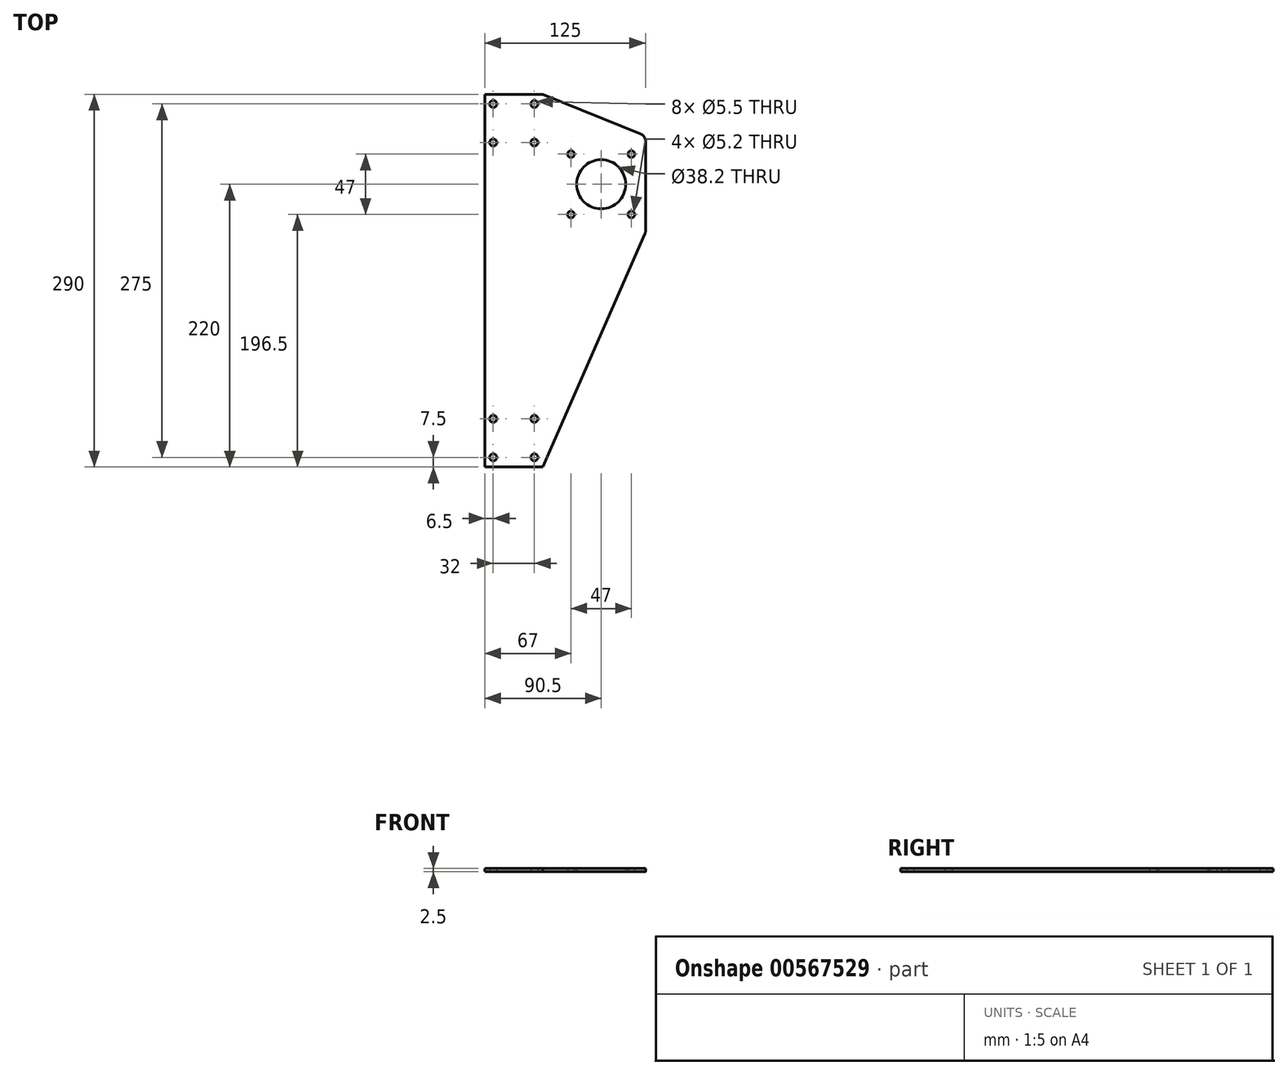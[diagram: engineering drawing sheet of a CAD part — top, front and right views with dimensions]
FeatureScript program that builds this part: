
annotation { "Feature Type Name" : "Feature", "Feature Type Description" : "" }
export const myFeature = defineFeature(function(context is Context, id is Id, definition is map)
    precondition{}
    {
        {
            var Q0;
            Q0=qCreatedBy(makeId("Top.planeOp"),FACE);
            var sketch = newSketch(context, id + "F0", { "sketchPlane" : qUnion([Q0])});
            skLineSegment(sketch, "E0", {"start": v(0, 70) * mm, "end": v(-22.5, 70) * mm});
            skLineSegment(sketch, "E1", {"start": v(-22.5, 70) * mm, "end": v(-22.5, 0) * mm});
            skLineSegment(sketch, "E2", {"start": v(-22.5, 0) * mm, "end": v(-22.5, -220) * mm});
            skLineSegment(sketch, "E3", {"start": v(-22.5, -220) * mm, "end": v(22.5, -220) * mm});
            skLineSegment(sketch, "E4", {"start": v(22.5, -220) * mm, "end": v(102, -38.7) * mm});
            skLineSegment(sketch, "E5", {"start": v(102.5, -36.29) * mm, "end": v(102.5, 33.64) * mm});
            skLineSegment(sketch, "E6", {"start": v(98.75, 39.2) * mm, "end": v(22.5, 70) * mm});
            skLineSegment(sketch, "E7", {"start": v(22.5, 70) * mm, "end": v(0, 70) * mm});
            skPoint(sketch, "E8.visualSharp", {"position": v(102.5, 37.69) * mm});
            skArc(sketch, "E8.filletArc", {"start": v(102.5, 33.64) * mm, "mid": v(101.47, 37) * mm, "end": v(98.75, 39.2) * mm});
            skPoint(sketch, "E9.visualSharp", {"position": v(102.5, -37.55) * mm});
            skArc(sketch, "E9.filletArc", {"start": v(102, -38.7) * mm, "mid": v(102.37, -37.52) * mm, "end": v(102.5, -36.29) * mm});
            skSolve(sketch);
        }
        {
            var Q0;
            Q0=qCreatedBy(makeId("Top.planeOp"),FACE);
            var sketch = newSketch(context, id + "F1", { "sketchPlane" : qUnion([Q0])});
            skCircle(sketch, "E10", {"center": v(68, 0) * mm, "radius": 19.1 * mm});
            skCircle(sketch, "E11", {"center": v(44.5, 23.5) * mm, "radius": 2.6 * mm});
            skCircle(sketch, "E12.MirrorC", {"center": v(44.5, -23.5) * mm, "radius": 2.6 * mm});
            skCircle(sketch, "E13", {"center": v(91.5, 23.5) * mm, "radius": 2.6 * mm});
            skCircle(sketch, "E14.MirrorC", {"center": v(91.5, -23.5) * mm, "radius": 2.6 * mm});
            skLineSegment(sketch, "E15.bottom", {"start": v(91.5, 23.5) * mm, "end": v(44.5, 23.5) * mm, "construction": true});
            skLineSegment(sketch, "E15.top", {"start": v(91.5, -23.5) * mm, "end": v(44.5, -23.5) * mm, "construction": true});
            skLineSegment(sketch, "E15.left", {"start": v(91.5, 23.5) * mm, "end": v(91.5, -23.5) * mm, "construction": true});
            skLineSegment(sketch, "E15.right", {"start": v(44.5, 23.5) * mm, "end": v(44.5, -23.5) * mm, "construction": true});
            skSolve(sketch);
        }
        {
            var Q0;
            Q0=qCreatedBy(makeId("Top.planeOp"),FACE);
            var sketch = newSketch(context, id + "F2", { "sketchPlane" : qUnion([Q0])});
            skCircle(sketch, "E16", {"center": v(-16, 62.5) * mm, "radius": 2.75 * mm});
            skCircle(sketch, "E17", {"center": v(-16, 32.5) * mm, "radius": 2.75 * mm});
            skCircle(sketch, "E18.MirrorC", {"center": v(16, 62.5) * mm, "radius": 2.75 * mm});
            skCircle(sketch, "E19.MirrorC", {"center": v(16, 32.5) * mm, "radius": 2.75 * mm});
            skLineSegment(sketch, "E20.bottom", {"start": v(-16, 32.5) * mm, "end": v(16, 32.5) * mm, "construction": true});
            skLineSegment(sketch, "E20.top", {"start": v(-16, 62.5) * mm, "end": v(16, 62.5) * mm, "construction": true});
            skLineSegment(sketch, "E20.left", {"start": v(-16, 32.5) * mm, "end": v(-16, 62.5) * mm, "construction": true});
            skLineSegment(sketch, "E20.right", {"start": v(16, 32.5) * mm, "end": v(16, 62.5) * mm, "construction": true});
            skSolve(sketch);
        }
        {
            var Q0;
            Q0=qCreatedBy(makeId("Top.planeOp"),FACE);
            var sketch = newSketch(context, id + "F3", { "sketchPlane" : qUnion([Q0])});
            skCircle(sketch, "E21", {"center": v(-16, -212.5) * mm, "radius": 2.75 * mm});
            skLineSegment(sketch, "E22.bottom", {"start": v(-16, -212.5) * mm, "end": v(16, -212.5) * mm, "construction": true});
            skLineSegment(sketch, "E22.top", {"start": v(-16, -182.5) * mm, "end": v(16, -182.5) * mm, "construction": true});
            skLineSegment(sketch, "E22.left", {"start": v(-16, -212.5) * mm, "end": v(-16, -182.5) * mm, "construction": true});
            skLineSegment(sketch, "E22.right", {"start": v(16, -212.5) * mm, "end": v(16, -182.5) * mm, "construction": true});
            skCircle(sketch, "E23.0.1.0", {"center": v(-16, -182.5) * mm, "radius": 2.75 * mm});
            skCircle(sketch, "E23.1.0.0", {"center": v(16, -212.5) * mm, "radius": 2.75 * mm});
            skCircle(sketch, "E23.1.1.0", {"center": v(16, -182.5) * mm, "radius": 2.75 * mm});
            skSolve(sketch);
        }
        {
            var Q0;
            Q0=makeQuery(id+"F0.imprint","IMPRINT",FACE,{"disambiguationData":[TD([[makeQuery(id+"F0.imprint","IMPRINT",EDGE,{"derivedFrom":sQuery(id+"F0.wireOp",EDGE,"E0")}),1.0]])]});
            extrude(context, id + "F4", {"entities" : qUnion([Q0]), "depth" : 2.5 * mm, "offsetDistance" : 25 * mm});
        }
        {
            var Q0;
            Q0 = qSketchRegion(id + "F3", true);
            var Q1;
            Q1 = qSketchRegion(id + "F1", true);
            var Q2;
            Q2 = qSketchRegion(id + "F2", true);
            extrude(context, id + "F5", {"entities" : qUnion([Q0, Q1, Q2]), "operationType" : NewBodyOperationType.REMOVE, "depth" : 2.5 * mm, "offsetDistance" : 25 * mm});
        }
    });
